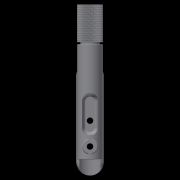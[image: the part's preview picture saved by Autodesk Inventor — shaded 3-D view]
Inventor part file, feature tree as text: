
AUTODESK INVENTOR PART (.ipt)
format: ipt  version: 2020 (Build 240168000, 168)  size: 19,166,208 bytes
history: native  units: in
note: dims shown in document units (in); Inventor stores cm internally (conversion verified against a paired STEP export)
features: other x23, extrude x12, fillet x5, projected_geometry x3, loft x2, pattern_circular x1, mirror x1, imported_body x1
ambient origin geometry x8: Origin, YZ Plane, XZ Plane, XY Plane, X Axis, Y Axis, Z Axis, Center Point
bodies: Solid1 (feature_tree), Solid2 (feature_tree), Solid3 (feature_tree), Solid6 (feature_tree), Solid4 (feature_tree), Solid5 (feature_tree)
feature tree (48):
  other  "strandberg-headless-tuner"
  other  "TunerTopView"
  other  "TunerFrontView"
  other  "TunerKnobPlane"
  other  "TunerKnobSep"
  other  "TunerEndPlane"
  other  "TunerEndProfile"
  loft  "TunerLoftFeature"
  loft  "TunerKnobLoftFeature"
  extrude  "TunerKnobSepFeature"  TaperAngle=0.0deg  [1 undecoded]
  fillet  "TunerFilletsFeature"  [1 undecoded]
  extrude  "TunerIndentFeature"  TaperAngle=0.0deg  [1 undecoded]
  fillet  "TunerIndentFillets1Feature"  Radius=0.03in
  fillet  "TunerIndentFillets2Feature"  Radius=0.01in
  other  "TunerIndentSubtractFeature"
  other  "TunderIndentProfile"
  extrude  "TunerHoleFeature"  Depth=0.05in
  extrude  "TunerHolesFeature"  Depth=0.05in
  other  "CountersinkPlane"
  extrude  "CountersinkFeature"  Depth=0.15in
  extrude  "BaseFeature"  Depth=0.25in TaperAngle=0.0deg
  extrude  "BaseExtendFeature"  Depth=0.12in
  extrude  "BaseFlareFeature"  Depth=0.1in
  fillet  "BaseFlareFilletsFeature"  Radius=1.8in
  extrude  "BaseHolesFeature"  Depth=0.4in
  other  "KnobSplitFeature"
  other  "KnurleCoilFeature"
  pattern_circular  "KnurleCoilRepeatFeature"  [2 undecoded]
  other  "KnobMidPlane"
  mirror  "KnurleMirrorFeature"
  extrude  "StringSaddleFeature"  Depth=0.2in TaperAngle=0.0deg
  extrude  "SaddleStringFeature"  [1 undecoded]
  fillet  "SaddleFilletFeature"  Radius=0.25in
  other  "CombineFeature"
  extrude  "MountHoleFeature"  Depth=1.0in TaperAngle=0.0deg
  other  "Edges1"
  other  "TunerIndent"
  projected_geometry  "Projected Loop1"
  other  "Countersink"
  imported_body  "Base"
  other  "BaseExtend"
  projected_geometry  "Projected Loop2"
  other  "BaseFlare"
  other  "BaseHoles"
  other  "KnurleCoil"
  projected_geometry  "Projected Loop3"
  other  "StringSaddle"
  other  "SaddleString"
note: 6 required parameter values undecoded (feature->parameter linkage not recoverable at this tier; creation-order binding heuristic only, values carry confidence <= 0.55)
